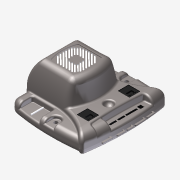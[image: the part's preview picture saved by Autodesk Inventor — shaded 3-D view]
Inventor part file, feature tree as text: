
AUTODESK INVENTOR PART (.ipt)
format: ipt  version: 2014 SP2 (Build 180246200, 246)  size: 8,239,104 bytes
history: native  units: mm
features: extrude x8, sketch x6, mirror x3, other x3, plane x2, imported_body x1
ambient origin geometry x8: Origin, YZ Plane, XZ Plane, XY Plane, X Axis, Y Axis, Z Axis, Center Point
bodies: Solid1 (feature_tree)
feature tree (23):
  imported_body  "Base1"
  sketch  "Sketch1"  dims[d14=193.04mm d50=0.9144mm]
  extrude  "Extrusion2"  Depth=0.9144mm
  plane  "Work Plane1"
  mirror  "Mirror1"
  extrude  "Extrusion3"  Depth=1.467403mm
  sketch  "Sketch2"  dims[d57=1.467403mm d58=1.467403mm]
  extrude  "Extrusion4"  Depth=1.467403mm
  extrude  "Extrusion6"  Depth=1.467403mm
  extrude  "Extrusion7"  Depth=1.27mm TaperAngle=0.0deg
  mirror  "Mirror2"
  extrude  "Extrusion8"  Depth=1.27mm TaperAngle=0.0deg
  mirror  "Mirror3"
  sketch  "Sketch5"  dims[d61=1.467403mm d62=1.467403mm]
  other  "Work Axis1"
  extrude  "Extrusion9"  Depth=1.27mm
  plane  "Work Plane2"
  extrude  "Extrusion10"  Depth=1.27mm TaperAngle=0.0deg
  other  "Image1"
  sketch  "Sketch4"  dims[d59=1.467403mm d60=1.467403mm]
  sketch  "Sketch6"  dims[d63=1.467403mm d66=1.27mm d67=0.0mm]
  sketch  "Sketch7"  dims[d70=90.0deg d71=1.27mm d72=0.0mm d73=9.7282mm d75=0.762mm d76=0.0mm d77=0.762mm d80=2.54mm d81=0.0mm d82=0.254mm d83=0.0mm d84=1.016mm d85=0.0mm d86=1.27mm d87=2.286mm d88=4.572mm d89=4.572mm d90=3.81mm d91=0.0mm d92=-15.24mm d105=129.575698mm d160=0.254mm d162=1.27mm d169=0.635mm d182=1.27mm d183=0.0mm]
  other  "Image2"
